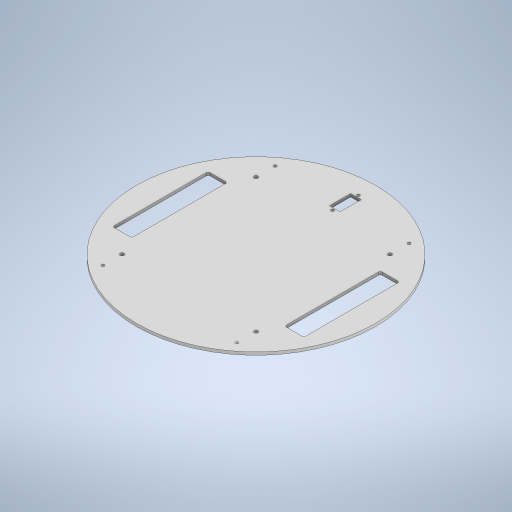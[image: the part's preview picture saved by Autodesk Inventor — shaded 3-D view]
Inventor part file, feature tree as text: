
AUTODESK INVENTOR PART (.ipt)
format: ipt  version: 2023.3 (Build 273359000, 359)  size: 285,696 bytes
history: native  units: mm
features: extrude x1, sketch x1
ambient origin geometry x8: Origin, YZ Plane, XZ Plane, XY Plane, X Axis, Y Axis, Z Axis, Center Point
bodies: Body1 (feature_tree)
feature tree (2):
  extrude  "Extrusion6"  [1 undecoded]
  sketch  "Sketch1"  dims[d33=3.0mm d34=0.0mm]
note: 1 required parameter value undecoded (feature->parameter linkage not recoverable at this tier; creation-order binding heuristic only, values carry confidence <= 0.55)
